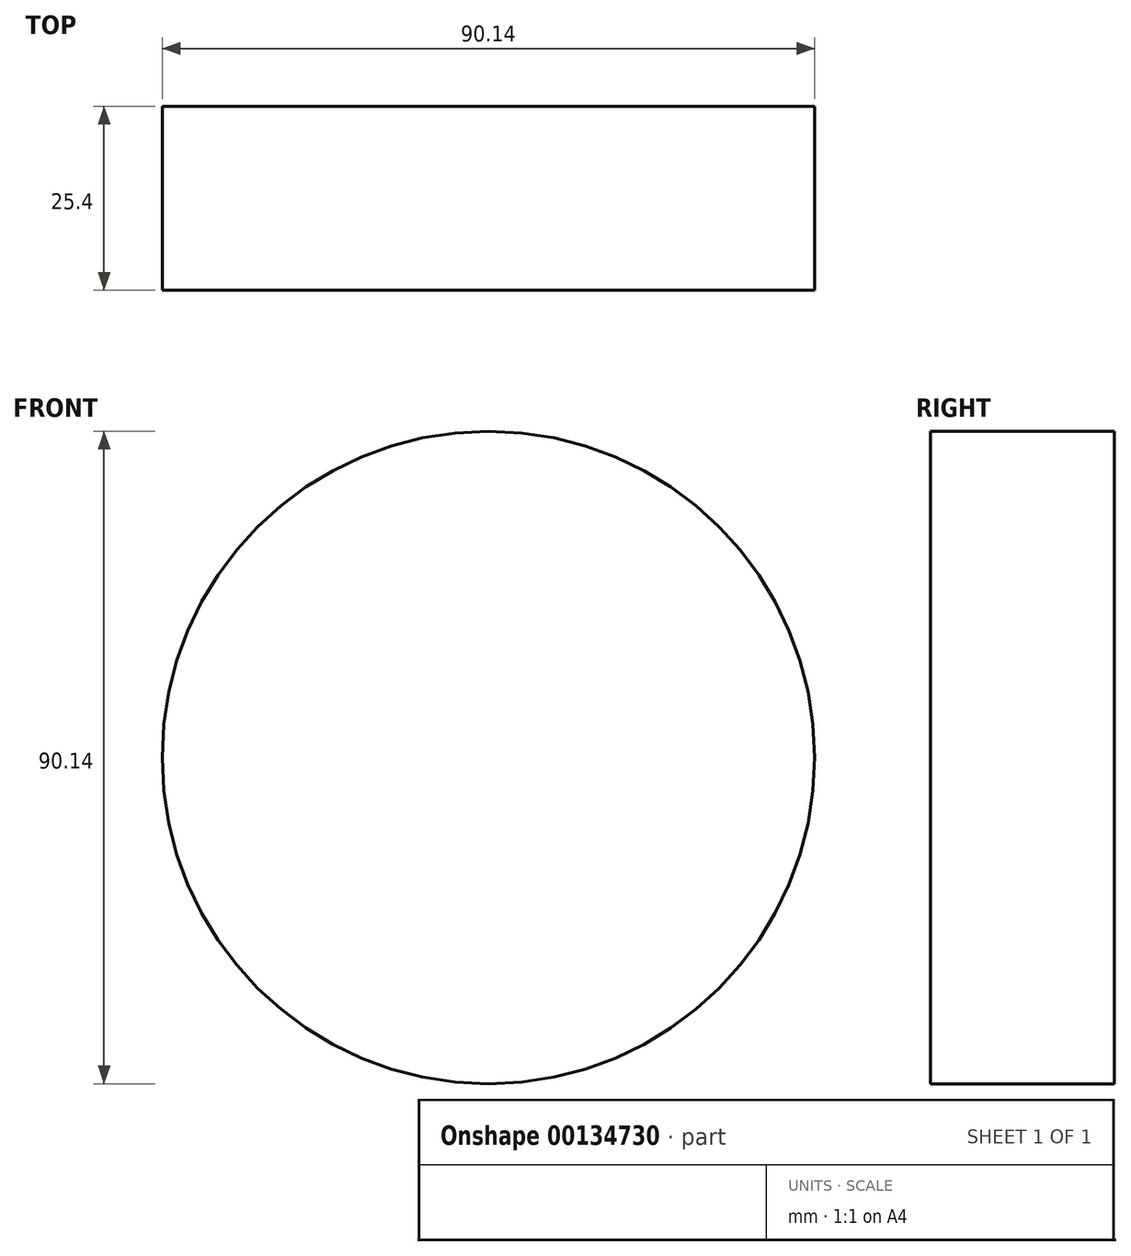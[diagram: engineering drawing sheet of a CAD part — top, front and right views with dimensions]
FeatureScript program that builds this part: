
annotation { "Feature Type Name" : "Feature", "Feature Type Description" : "" }
export const myFeature = defineFeature(function(context is Context, id is Id, definition is map)
    precondition{}
    {
        {
            var Q0;
            Q0=qCreatedBy(makeId("Front.planeOp"),FACE);
            var sketch = newSketch(context, id + "F0", { "sketchPlane" : qUnion([Q0])});
            skCircle(sketch, "E0", {"center": v(-18.55, 40.13) * mm, "radius": 45.07 * mm});
            skSolve(sketch);
        }
        {
            var Q0;
            Q0=makeQuery(id+"F0.imprint","IMPRINT",FACE,{"disambiguationData":[TD([[makeQuery(id+"F0.imprint","IMPRINT",EDGE,{"derivedFrom":sQuery(id+"F0.wireOp",EDGE,"E0")}),1.0]])]});
            extrude(context, id + "F1", {"entities" : qUnion([Q0]), "depth" : 25.4 * mm});
        }
    });
